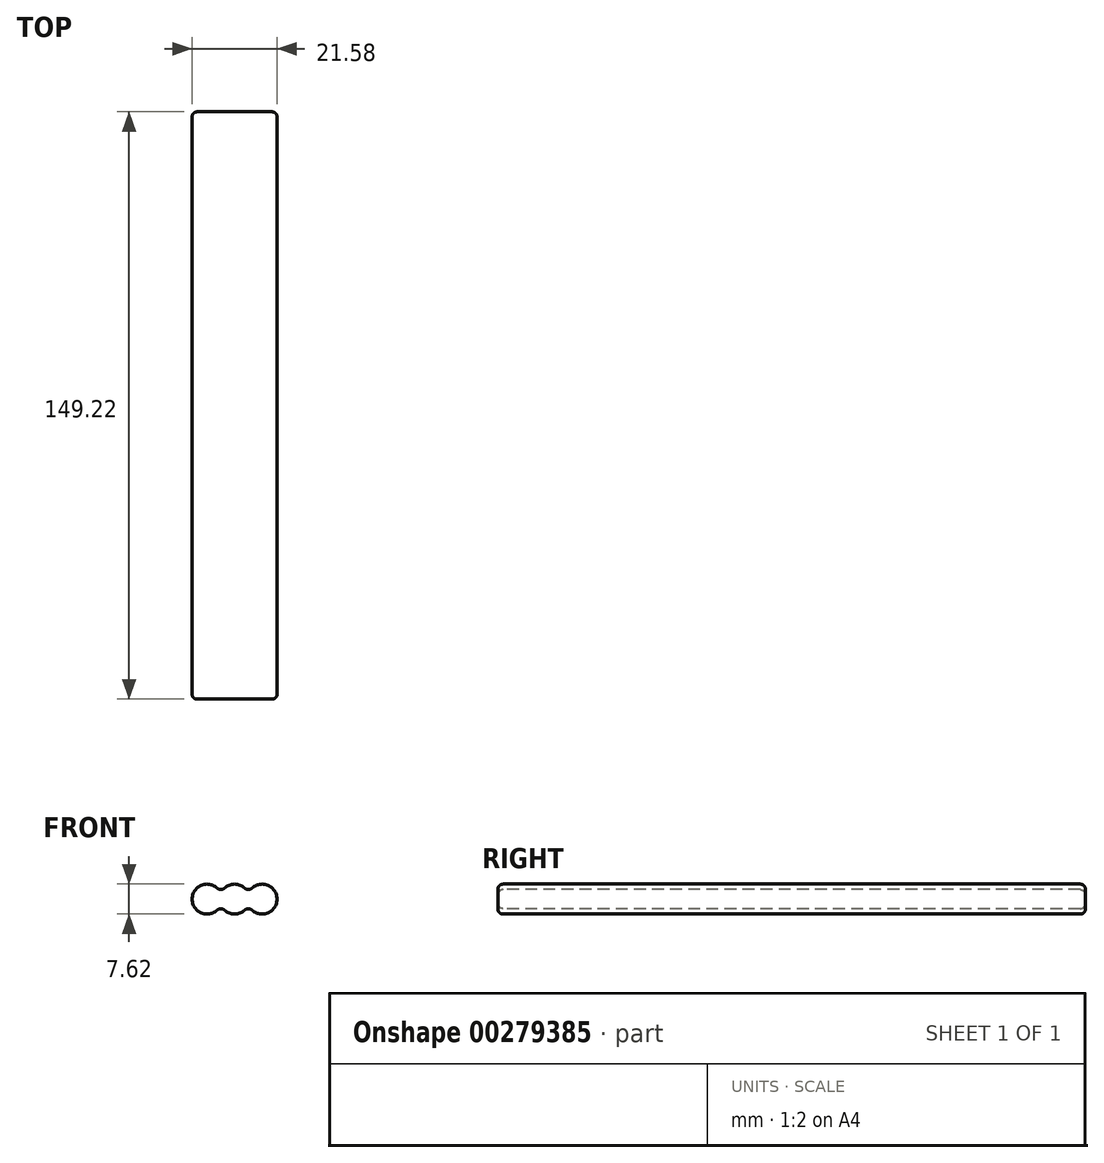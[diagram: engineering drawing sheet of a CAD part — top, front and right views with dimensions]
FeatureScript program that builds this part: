
annotation { "Feature Type Name" : "Feature", "Feature Type Description" : "" }
export const myFeature = defineFeature(function(context is Context, id is Id, definition is map)
    precondition{}
    {
        {
            var Q0;
            Q0=qCreatedBy(makeId("Front.planeOp"),FACE);
            var sketch = newSketch(context, id + "F0", { "sketchPlane" : qUnion([Q0])});
            skArc(sketch, "E0", {"start": v(3.5, 1.52) * mm, "mid": v(0, 3.81) * mm, "end": v(-3.5, 1.52) * mm});
            skArc(sketch, "E1", {"start": v(3.5, -1.52) * mm, "mid": v(10.8, 0) * mm, "end": v(3.5, 1.52) * mm});
            skArc(sketch, "E2", {"start": v(-3.5, 1.52) * mm, "mid": v(-10.8, 0) * mm, "end": v(-3.5, -1.52) * mm});
            skLineSegment(sketch, "E3", {"start": v(-6.99, 0) * mm, "end": v(6.99, 0) * mm, "construction": true});
            skArc(sketch, "E4.trimOffspring", {"start": v(-3.5, -1.52) * mm, "mid": v(0, -3.81) * mm, "end": v(3.5, -1.52) * mm});
            skSolve(sketch);
        }
        {
            var Q0;
            Q0=makeQuery(id+"F0.imprint","IMPRINT",FACE,{"disambiguationData":[TD([[makeQuery(id+"F0.imprint","IMPRINT",EDGE,{"derivedFrom":sQuery(id+"F0.wireOp",EDGE,"E0")}),1.0]])]});
            extrude(context, id + "F1", {"entities" : qUnion([Q0]), "endBound" : BoundingType.SYMMETRIC, "depth" : 149.22 * mm});
        }
        {
            var Q0;
            Q0=makeQuery(id+"F1.opExtrude","SWEPT_EDGE",EDGE,{"disambiguationData":[OSD([sQuery(id+"F0.wireOp",EDGE,"E0"),sQuery(id+"F0.wireOp",EDGE,"E2")])]});
            var Q1;
            Q1=makeQuery(id+"F1.opExtrude","SWEPT_EDGE",EDGE,{"disambiguationData":[OSD([sQuery(id+"F0.wireOp",EDGE,"E0"),sQuery(id+"F0.wireOp",EDGE,"E1")])]});
            var Q2;
            Q2=makeQuery(id+"F1.opExtrude","SWEPT_EDGE",EDGE,{"disambiguationData":[OSD([sQuery(id+"F0.wireOp",EDGE,"E2"),sQuery(id+"F0.wireOp",EDGE,"E4.trimOffspring")])]});
            var Q3;
            Q3=makeQuery(id+"F1.opExtrude","SWEPT_EDGE",EDGE,{"disambiguationData":[OSD([sQuery(id+"F0.wireOp",EDGE,"E1"),sQuery(id+"F0.wireOp",EDGE,"E4.trimOffspring")])]});
            var Q4;
            Q4=makeQuery(id+"F1.opExtrude","CAP_FACE",FACE,{"disambiguationData":[OSD([sQuery(id+"F0.wireOp",EDGE,"E0"),sQuery(id+"F0.wireOp",EDGE,"E1"),sQuery(id+"F0.wireOp",EDGE,"E2"),sQuery(id+"F0.wireOp",EDGE,"E4.trimOffspring")])],"isStart":true});
            var Q5;
            Q5=makeQuery(id+"F1.opExtrude","CAP_FACE",FACE,{"disambiguationData":[OSD([sQuery(id+"F0.wireOp",EDGE,"E0"),sQuery(id+"F0.wireOp",EDGE,"E1"),sQuery(id+"F0.wireOp",EDGE,"E2"),sQuery(id+"F0.wireOp",EDGE,"E4.trimOffspring")])],"isStart":false});
            fillet(context, id + "F2", {"entities" : qUnion([Q0, Q1, Q2, Q3, Q4, Q5]), "radius" : 1.27 * mm, "tangentPropagation" : true, "allowEdgeOverflow" : false});
        }
    });
